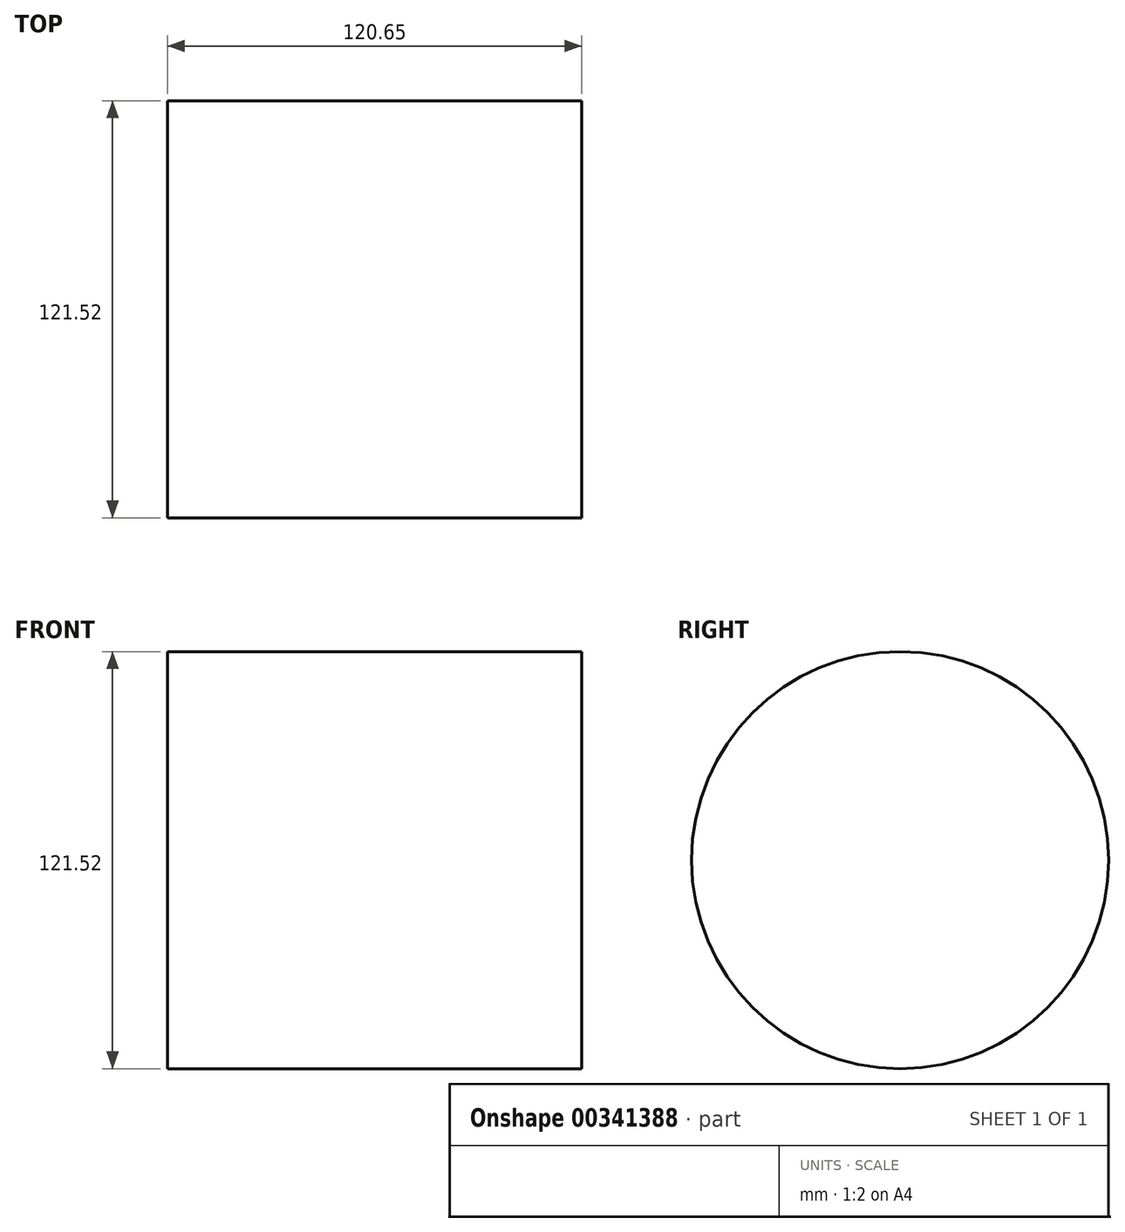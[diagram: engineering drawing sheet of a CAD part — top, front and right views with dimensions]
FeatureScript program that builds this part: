
annotation { "Feature Type Name" : "Feature", "Feature Type Description" : "" }
export const myFeature = defineFeature(function(context is Context, id is Id, definition is map)
    precondition{}
    {
        {
            var Q0;
            Q0=qCreatedBy(makeId("Right.planeOp"),FACE);
            var sketch = newSketch(context, id + "F0", { "sketchPlane" : qUnion([Q0])});
            skCircle(sketch, "E0", {"center": v(0, 0) * mm, "radius": 60.76 * mm});
            skSolve(sketch);
        }
        {
            var Q0;
            Q0 = qSketchRegion(id + "F0", true);
            extrude(context, id + "F1", {"entities" : qUnion([Q0]), "depth" : 59.69 * mm, "hasSecondDirection" : true, "secondDirectionOppositeDirection" : true, "secondDirectionDepth" : 60.96 * mm});
        }
    });
